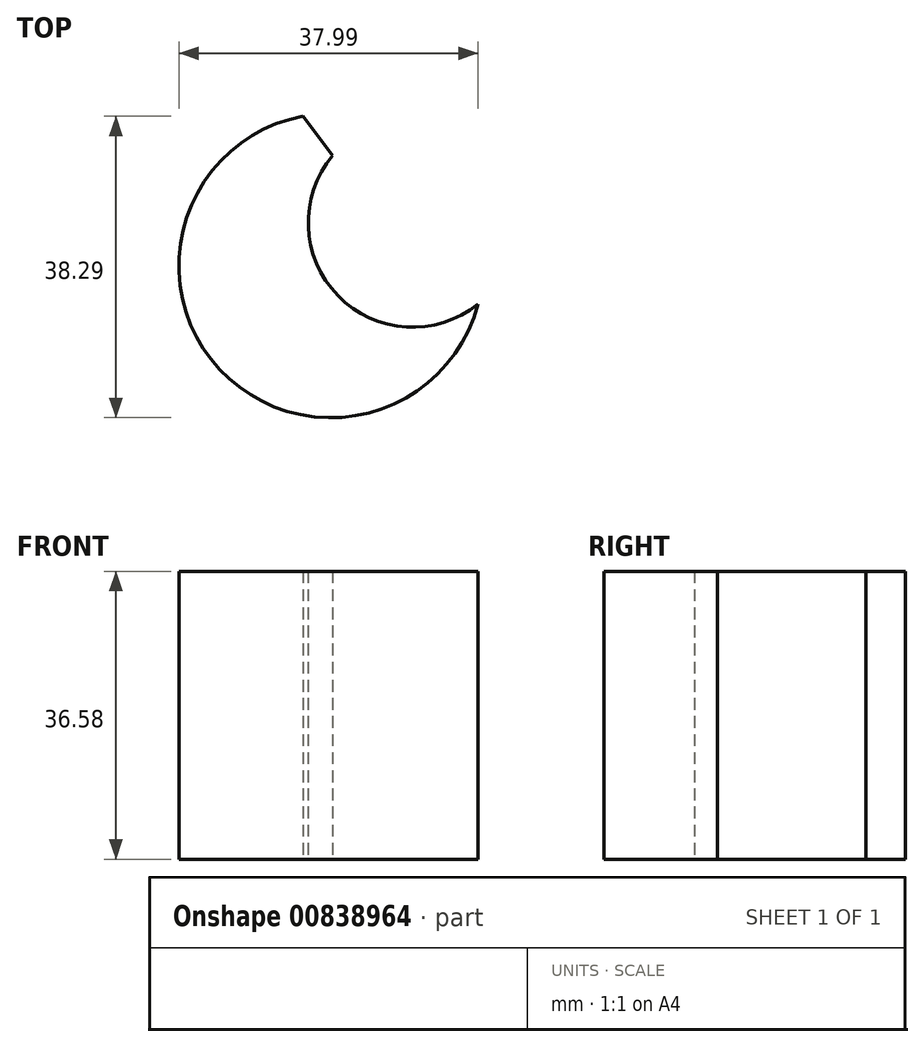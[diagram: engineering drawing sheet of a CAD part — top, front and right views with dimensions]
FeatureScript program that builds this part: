
annotation { "Feature Type Name" : "Feature", "Feature Type Description" : "" }
export const myFeature = defineFeature(function(context is Context, id is Id, definition is map)
    precondition{}
    {
        {
            var Q0;
            Q0=qCreatedBy(makeId("Top.planeOp"),FACE);
            var sketch = newSketch(context, id + "F0", { "sketchPlane" : qUnion([Q0])});
            skArc(sketch, "E0", {"start": v(0, 12.78) * mm, "mid": v(-4.48, -10.56) * mm, "end": v(16.8, 0) * mm});
            skLineSegment(sketch, "E1", {"start": v(0, 12.78) * mm, "end": v(3.54, 0) * mm});
            skLineSegment(sketch, "E2", {"start": v(3.54, 0) * mm, "end": v(16.8, 0) * mm});
            skLineSegment(sketch, "E3.0", {"start": v(-10.39, 13.52) * mm, "end": v(2.32, -3.2) * mm});
            skArc(sketch, "E3.1", {"start": v(-10.39, 13.52) * mm, "mid": v(-18.28, -21.02) * mm, "end": v(12.34, -3.19) * mm});
            skLineSegment(sketch, "E3.2", {"start": v(2.32, -3.2) * mm, "end": v(12.34, -3.19) * mm});
            skLineSegment(sketch, "E4", {"start": v(21.52, 62.87) * mm, "end": v(38.37, 62.87) * mm});
            skLineSegment(sketch, "E5", {"start": v(62.47, 79.52) * mm, "end": v(74.82, 65.88) * mm});
            skLineSegment(sketch, "E6.0", {"start": v(55.25, 57.22) * mm, "end": v(66, 45.35) * mm});
            skLineSegment(sketch, "E6.1", {"start": v(21.52, 42.55) * mm, "end": v(32, 42.55) * mm});
            skLineSegment(sketch, "E7.0", {"start": v(61.33, 71.31) * mm, "end": v(73.72, 57.63) * mm});
            skLineSegment(sketch, "E8", {"start": v(-56.27, 39.3) * mm, "end": v(-24.82, 39.3) * mm});
            skLineSegment(sketch, "E9", {"start": v(-28.9, 70.9) * mm, "end": v(-19.37, 58.03) * mm});
            skLineSegment(sketch, "E10.0", {"start": v(-62.82, 32.95) * mm, "end": v(-19.9, 32.95) * mm});
            skLineSegment(sketch, "E11.0", {"start": v(-32.88, 65.6) * mm, "end": v(-23.36, 52.74) * mm});
            skLineSegment(sketch, "E12", {"start": v(-48.42, 27.98) * mm, "end": v(-23.52, 27.98) * mm});
            skLineSegment(sketch, "E13.bottom", {"start": v(41.39, -25.3) * mm, "end": v(58.25, -19.81) * mm});
            skLineSegment(sketch, "E13.right", {"start": v(58.25, -19.81) * mm, "end": v(55.63, -28.96) * mm});
            skLineSegment(sketch, "E14.0", {"start": v(79.82, 2.56) * mm, "end": v(67.94, -39.02) * mm});
            skLineSegment(sketch, "E14.1", {"start": v(27.9, -14.35) * mm, "end": v(79.82, 2.56) * mm});
            skLineSegment(sketch, "E14.2", {"start": v(27.9, -14.35) * mm, "end": v(27.9, -39.02) * mm});
            skLineSegment(sketch, "E14.3", {"start": v(27.9, -39.02) * mm, "end": v(67.94, -39.02) * mm});
            skLineSegment(sketch, "E15", {"start": v(-57.6, -30.45) * mm, "end": v(-33.96, -30.45) * mm});
            skLineSegment(sketch, "E16", {"start": v(-31.62, -48.73) * mm, "end": v(-19.93, -57.4) * mm});
            skLineSegment(sketch, "E17", {"start": v(-19.93, -57.4) * mm, "end": v(-29.56, -67.7) * mm});
            skLineSegment(sketch, "E18.0", {"start": v(6.65, -54.97) * mm, "end": v(-16.56, -79.84) * mm});
            skLineSegment(sketch, "E18.1", {"start": v(-21.03, -34.45) * mm, "end": v(6.65, -54.97) * mm});
            skFitSpline(sketch, "E19", {"points": [v(48.14, 30.23) * mm, v(29.58, 20.5) * mm, v(16.17, 33.17) * mm, v(12, 20.58) * mm], "startDerivative": vector(-52.1, -50.11) * mm, "endDerivative": vector(-8.95, -66.71) * mm});
            skLineSegment(sketch, "E20", {"start": v(55.63, -28.96) * mm, "end": v(42.3, -30.07) * mm});
            skLineSegment(sketch, "E21", {"start": v(36.64, -51.55) * mm, "end": v(62.3, -51.55) * mm});
            skLineSegment(sketch, "E22", {"start": v(46.28, -56.46) * mm, "end": v(65.74, -56.46) * mm});
            skSolve(sketch);
        }
        {
            var Q0;
            Q0=makeQuery(id+"F0.imprint","IMPRINT",FACE,{"disambiguationData":[TD([[makeQuery(id+"F0.imprint","IMPRINT",EDGE,{"derivedFrom":sQuery(id+"F0.wireOp",EDGE,"E3.0")}),-1.0]])]});
            extrude(context, id + "F1", {"entities" : qUnion([Q0]), "depth" : 36.58 * mm, "offsetDistance" : 25.4 * mm});
        }
    });
